# Revit family: CADS_AIRFLOWdev_AirflexPro_Round_90DegCeilingOutlet_Supply
name_source: partatom
category: Duct Fittings
units: mm (PartAtom-declared; Revit-internal decimal feet)

## family parameters
Always vertical = Yes
Cut with Voids When Loaded = No
Part Type = Wye
Round Connector Dimension = Use Diameter
Shared = No
Work Plane-Based = No

## types (3) — shared parameters
6MonthlyMaintenance = Visually inspect system, clean the fan and ducting if necessary
AF_Body = AF_Grey
AirflowRateRange = 18.0 L/s
AssemblyPlace = UNKNOWN
AssetType = FIXED
CEApproval = Yes
Color = Silver
DurationUnit = Year
ExpectedServiceLife = 10
Finish = Lacquer
FireControlPanelLinks = No
Fitting Type = Ignore
Grade = Stainless
GrossWeight = 1.10 kg
ISO140001 = Yes
ISO90001 = Yes
IsExtendedWarranty = No
LongitudinalSeam = None
Manufacturer = Airflow Developments Ltd
ManufacturerAddress = Aidelle House
Lancaster Road
Cressex Business Park
High Wycombe
Bucks
HP123QP
ManufacturerTelephone = 01494 525252
ManufacturerWebsite = www.airflow.com
Material = Steel
NBSCode = 45-80-50/394 Ventilation ducts
NominalHeight = 385 mm
NominalLength = 245 mm
NominalWidth = 190 mm
PassiveHouseApproval = No
PointOfContact = Airflow Developments Ltd
ProductLiterature = https://www.airflow.com
ProductionYear = 2017
Quantity = 1
RedDotDesignAward = No
ReplacementCost = 71.208
RunID = 0
SAPApproval = Yes
ServiceLifeDuration = 10
ServiceLifeType = EXPECTEDSERVICELIFE
Shape = Other
ShippingWeight = 1.32 kg
Size = 245x 190x  385
Status = New
TemperatureRange = up to 40°C
Uniclass2015 = Pr_30_59_96_92:Ventilation ducts
WarrantyGuarantor = Airflow Developments Ltd
WarrantyPeriod = 0
WorkingPressure = 3000.0 Pa
zero-valued in all types: CADS_Index

## per-type parameters (varying)
| type | Constituents | Features |
| CADS_AIRFLOWdev_AirFlex_Round_WallPlenum | Round 90o floor plenum for use with 9041174 | Round 90o floor plenum for use with 9041174 |
| CADS_AIRFLOWdev_AirflexPro_Round_90DegFloorOutlet_Supply | Round 90o floor plenum for use with 9041174 | Round 90o floor plenum for use with 9041174 |
| CADS_AIRFLOWdev_AirflexPro_Round_90Deg Ceiling Outlet_Supply | Round 90o ceiling plenum | Round 90o Ceiling Plenum |

## geometry (parser evidence)
native form markers: Blend x4, Sweep x1
no freeform markers — native parametric forms only
